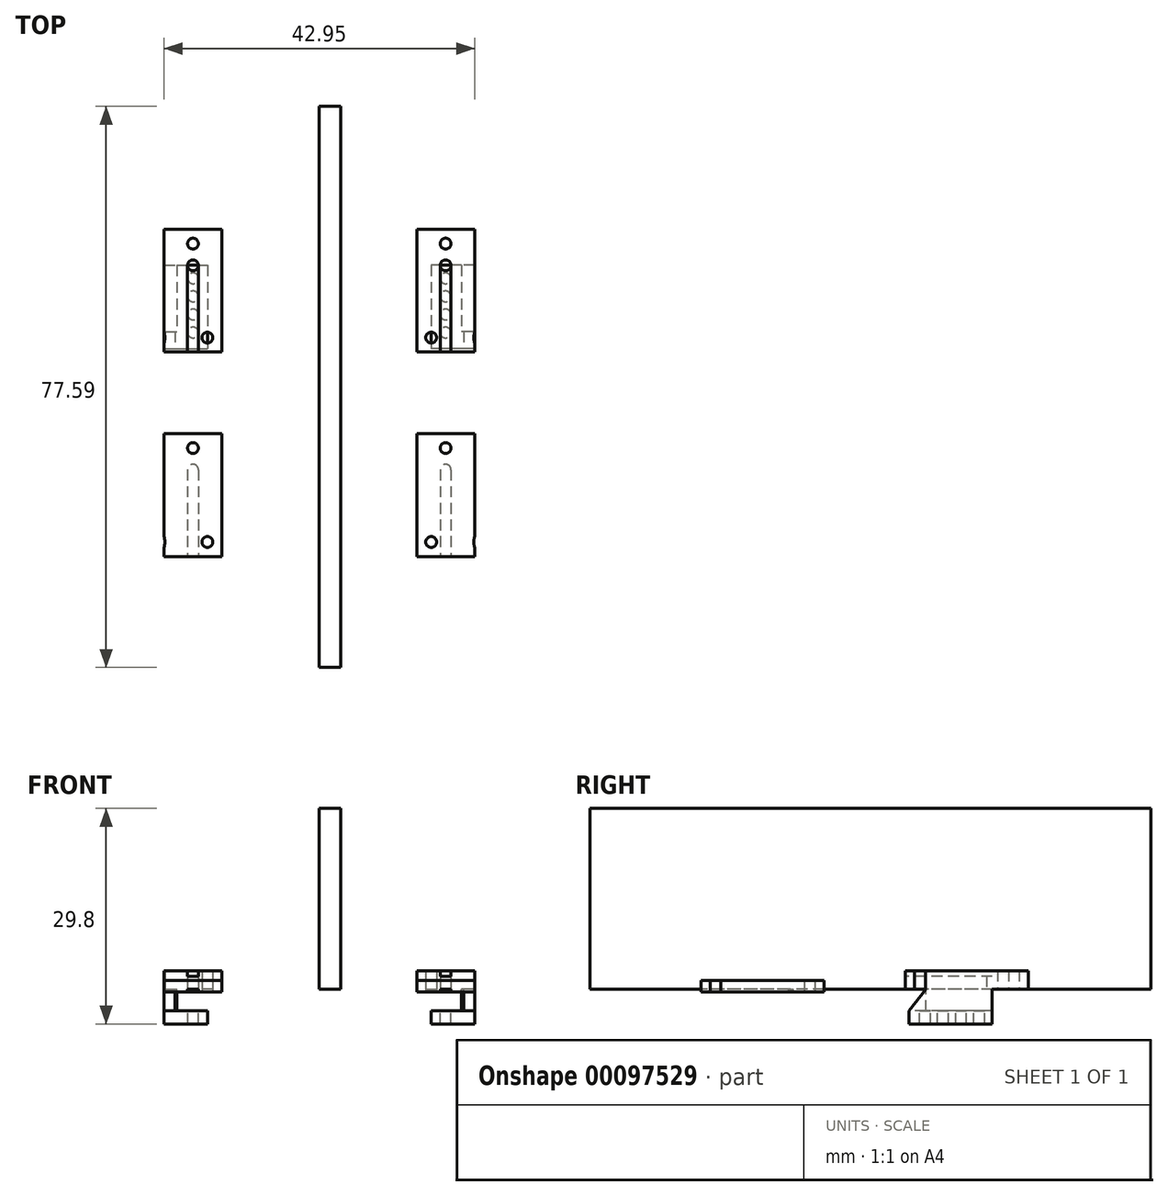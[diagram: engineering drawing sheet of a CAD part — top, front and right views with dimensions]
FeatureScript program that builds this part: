
annotation { "Feature Type Name" : "Feature", "Feature Type Description" : "" }
export const myFeature = defineFeature(function(context is Context, id is Id, definition is map)
    precondition{}
    {
        {
            var Q0;
            Q0=qCreatedBy(makeId("Top.planeOp"),FACE);
            var sketch = newSketch(context, id + "F0", { "sketchPlane" : qUnion([Q0])});
            skLineSegment(sketch, "E0.bottom", {"start": v(-5.2, 9) * mm, "end": v(2.8, 9) * mm});
            skLineSegment(sketch, "E0.top", {"start": v(-5.2, -8) * mm, "end": v(2.8, -8) * mm});
            skLineSegment(sketch, "E0.left", {"start": v(-5.2, 9) * mm, "end": v(-5.2, -5.26) * mm});
            skLineSegment(sketch, "E0.right", {"start": v(2.8, 9) * mm, "end": v(2.8, -8) * mm});
            skLineSegment(sketch, "E1", {"start": v(2.8, 9) * mm, "end": v(2.8, 11) * mm, "construction": true});
            skLineSegment(sketch, "E2", {"start": v(2.8, 11) * mm, "end": v(-1.2, 11) * mm, "construction": true});
            skLineSegment(sketch, "E3", {"start": v(-1.2, 11) * mm, "end": v(-1.2, 4) * mm, "construction": true});
            skCircle(sketch, "E4", {"center": v(-1.2, 4) * mm, "radius": 0.75 * mm});
            skLineSegment(sketch, "E5", {"start": v(-1.2, 9) * mm, "end": v(-1.2, 7) * mm, "construction": true});
            skCircle(sketch, "E6", {"center": v(-1.2, 7) * mm, "radius": 0.75 * mm});
            skLineSegment(sketch, "E7.bottom", {"start": v(2.8, -8) * mm, "end": v(0.8, -8) * mm, "construction": true});
            skLineSegment(sketch, "E7.top", {"start": v(2.8, -6) * mm, "end": v(0.8, -6) * mm, "construction": true});
            skLineSegment(sketch, "E7.left", {"start": v(2.8, -8) * mm, "end": v(2.8, -6) * mm, "construction": true});
            skLineSegment(sketch, "E7.right", {"start": v(0.8, -8) * mm, "end": v(0.8, -6) * mm, "construction": true});
            skCircle(sketch, "E8", {"center": v(0.8, -6) * mm, "radius": 0.75 * mm});
            skLineSegment(sketch, "E9", {"start": v(0.8, -6.76) * mm, "end": v(-5.2, -6.76) * mm, "construction": true});
            skLineSegment(sketch, "E10.MirrorCS", {"start": v(0.8, -5.26) * mm, "end": v(-5.2, -5.26) * mm, "construction": true});
            skArc(sketch, "E11", {"start": v(-5.2, -6.76) * mm, "mid": v(-5.1, -6) * mm, "end": v(-5.2, -5.26) * mm});
            skLineSegment(sketch, "E12.trimOffspring", {"start": v(-5.2, -6.76) * mm, "end": v(-5.2, -8) * mm});
            skLineSegment(sketch, "E13.0.1.0", {"start": v(0.8, -33.52) * mm, "end": v(-5.2, -33.52) * mm, "construction": true});
            skLineSegment(sketch, "E13.0.1.1", {"start": v(-5.2, -36.27) * mm, "end": v(2.8, -36.27) * mm});
            skLineSegment(sketch, "E13.0.1.2", {"start": v(0.8, -35.02) * mm, "end": v(-5.2, -35.02) * mm, "construction": true});
            skLineSegment(sketch, "E13.0.1.3", {"start": v(-1.2, -19.27) * mm, "end": v(-1.2, -21.27) * mm, "construction": true});
            skLineSegment(sketch, "E13.0.1.4", {"start": v(-5.2, -19.27) * mm, "end": v(-5.2, -33.52) * mm});
            skLineSegment(sketch, "E13.0.1.5", {"start": v(-5.2, -19.27) * mm, "end": v(2.8, -19.27) * mm});
            skLineSegment(sketch, "E13.0.1.6", {"start": v(2.8, -34.27) * mm, "end": v(0.8, -34.27) * mm, "construction": true});
            skCircle(sketch, "E13.0.1.7", {"center": v(0.8, -34.27) * mm, "radius": 0.75 * mm});
            skCircle(sketch, "E13.0.1.8", {"center": v(-1.2, -21.27) * mm, "radius": 0.75 * mm});
            skArc(sketch, "E13.0.1.9", {"start": v(-5.2, -35.02) * mm, "mid": v(-5.1, -34.27) * mm, "end": v(-5.2, -33.52) * mm});
            skLineSegment(sketch, "E13.0.1.10", {"start": v(2.8, -19.27) * mm, "end": v(2.8, -36.27) * mm});
            skLineSegment(sketch, "E13.0.1.12", {"start": v(0.8, -36.27) * mm, "end": v(0.8, -34.27) * mm, "construction": true});
            skLineSegment(sketch, "E13.0.1.13", {"start": v(2.8, -36.27) * mm, "end": v(0.8, -36.27) * mm, "construction": true});
            skLineSegment(sketch, "E13.0.1.14", {"start": v(2.8, -36.27) * mm, "end": v(2.8, -34.27) * mm, "construction": true});
            skLineSegment(sketch, "E13.0.1.15", {"start": v(-5.2, -35.02) * mm, "end": v(-5.2, -36.27) * mm});
            skLineSegment(sketch, "E13.direction1", {"start": v(-5.2, -5.26) * mm, "end": v(19.8, -5.26) * mm, "construction": true});
            skLineSegment(sketch, "E13.direction2", {"start": v(-5.2, -5.26) * mm, "end": v(-5.2, -33.52) * mm, "construction": true});
            skLineSegment(sketch, "E14", {"start": v(-1.2, -24.27) * mm, "end": v(2.8, -24.27) * mm, "construction": true});
            skCircle(sketch, "E15", {"center": v(-1.2, -24.27) * mm, "radius": 0.75 * mm});
            skLineSegment(sketch, "E16", {"start": v(-0.46, -24.27) * mm, "end": v(-0.46, -36.27) * mm});
            skLineSegment(sketch, "E17", {"start": v(-1.2, -24.27) * mm, "end": v(-1.2, -23.52) * mm, "construction": true});
            skLineSegment(sketch, "E18.MirrorCS", {"start": v(-1.96, -24.27) * mm, "end": v(-1.96, -36.27) * mm});
            skLineSegment(sketch, "E19.bottom", {"start": v(16.27, 25.97) * mm, "end": v(19.26, 25.97) * mm});
            skLineSegment(sketch, "E19.top", {"start": v(16.27, -51.62) * mm, "end": v(19.26, -51.62) * mm});
            skLineSegment(sketch, "E19.left", {"start": v(16.27, 25.97) * mm, "end": v(16.27, -51.62) * mm});
            skLineSegment(sketch, "E19.right", {"start": v(19.26, 25.97) * mm, "end": v(19.26, -51.62) * mm});
            skSolve(sketch);
        }
        {
            var Q0;
            Q0=makeQuery(id+"F0.imprint","IMPRINT",FACE,{"disambiguationData":[TD([[makeQuery(id+"F0.imprint","IMPRINT",EDGE,{"derivedFrom":sQuery(id+"F0.wireOp",EDGE,"E0.bottom")}),-1.0]])]});
            extrude(context, id + "F1", {"entities" : qUnion([Q0]), "depth" : 1.8 * mm});
        }
        {
            var Q0;
            Q0=makeQuery(id+"F1.opExtrude","CAP_FACE",FACE,{"disambiguationData":[OSD([sQuery(id+"F0.wireOp",EDGE,"E0.bottom"),sQuery(id+"F0.wireOp",EDGE,"E0.top"),sQuery(id+"F0.wireOp",EDGE,"E0.left"),sQuery(id+"F0.wireOp",EDGE,"E0.right"),sQuery(id+"F0.wireOp",EDGE,"E4")])],"isStart":false});
            var sketch = newSketch(context, id + "F2", { "sketchPlane" : qUnion([Q0])});
            skLineSegment(sketch, "E20", {"start": v(-1.2, 4) * mm, "end": v(8.32, 4) * mm, "construction": true});
            skLineSegment(sketch, "E21", {"start": v(-0.46, 4) * mm, "end": v(-0.46, -8) * mm});
            skLineSegment(sketch, "E22", {"start": v(-1.2, 4) * mm, "end": v(-1.2, 9) * mm, "construction": true});
            skLineSegment(sketch, "E23.MirrorCS", {"start": v(-1.96, 4) * mm, "end": v(-1.96, -8) * mm});
            skSolve(sketch);
        }
        {
            var Q0;
            {var subQ1=sQuery(id+"F2.wireOp",EDGE,"E21");Q0=makeQuery(id+"F2.imprint","IMPRINT",FACE,{"disambiguationData":[TD([[makeQuery(id+"F2.imprint","IMPRINT",EDGE,{"derivedFrom":subQ1}),1.0]])]});}
            extrude(context, id + "F3", {"entities" : qUnion([Q0]), "operationType" : NewBodyOperationType.ADD, "depth" : 0.75 * mm});
        }
        {
            var Q0;
            Q0=makeQuery(id+"F1.opExtrude","CAP_FACE",FACE,{"disambiguationData":[OSD([sQuery(id+"F0.wireOp",EDGE,"E0.bottom"),sQuery(id+"F0.wireOp",EDGE,"E0.top"),sQuery(id+"F0.wireOp",EDGE,"E0.left"),sQuery(id+"F0.wireOp",EDGE,"E0.right"),sQuery(id+"F0.wireOp",EDGE,"E4")])],"isStart":true});
            var sketch = newSketch(context, id + "F4", { "sketchPlane" : qUnion([Q0])});
            skLineSegment(sketch, "E24", {"start": v(-5.2, -9) * mm, "end": v(-3.7, -9) * mm, "construction": true});
            skPoint(sketch, "E24.endSnap0", {"position": v(-1.2, -9) * mm});
            skLineSegment(sketch, "E25", {"start": v(-5.2, 5.26) * mm, "end": v(-5.2, 5.16) * mm, "construction": true});
            skLineSegment(sketch, "E26", {"start": v(-5.2, 5.16) * mm, "end": v(-3.4, 5.16) * mm});
            skLineSegment(sketch, "E27", {"start": v(-5.2, -9) * mm, "end": v(-5.2, -4) * mm, "construction": true});
            skLineSegment(sketch, "E28", {"start": v(-5.2, -4) * mm, "end": v(-3.4, -4) * mm});
            skLineSegment(sketch, "E29", {"start": v(-3.4, -4) * mm, "end": v(-3.4, 5.16) * mm});
            skSolve(sketch);
        }
        {
            var Q0;
            Q0=makeQuery(id+"F0.imprint","IMPRINT",FACE,{"disambiguationData":[TD([[makeQuery(id+"F0.imprint","IMPRINT",EDGE,{"derivedFrom":sQuery(id+"F0.wireOp",EDGE,"E13.0.1.4")}),1.0]])]});
            var Q1;
            {var subQ0=sQuery(id+"F0.wireOp",EDGE,"MRaOlkRU-Fsrc-L5Ae-Ih45-m6OzS7PlfYht");Q1=makeQuery(id+"F0.imprint","IMPRINT",FACE,{"disambiguationData":[TD([[makeQuery(id+"F0.imprint","IMPRINT",EDGE,{"derivedFrom":subQ0}),1.0]])]});}
            var Q2;
            {var subQ0=sQuery(id+"F0.wireOp",EDGE,"E16");Q2=makeQuery(id+"F0.imprint","IMPRINT",FACE,{"disambiguationData":[TD([[makeQuery(id+"F0.imprint","IMPRINT",EDGE,{"derivedFrom":subQ0}),-1.0]])]});}
            var Q3;
            {var subQ0=sQuery(id+"F0.wireOp",EDGE,"E15");var subQ1=makeQuery(id+"F0.imprint","INTERSECT",VERTEX,{"derivedFrom":[subQ0,sQuery(id+"F0.wireOp",EDGE,"E16")]});Q3=makeQuery(id+"F0.imprint","IMPRINT",FACE,{"disambiguationData":[TD([[makeQuery(id+"F0.imprint","IMPRINT",EDGE,{"disambiguationData":[TD([[subQ1,-1.0]])],"derivedFrom":subQ0}),1.0]])]});}
            extrude(context, id + "F5", {"entities" : qUnion([Q0, Q1, Q2, Q3]), "depth" : 1.2 * mm});
        }
        {
            var Q0;
            Q0=makeQuery(id+"F0.imprint","IMPRINT",FACE,{"disambiguationData":[TD([[makeQuery(id+"F0.imprint","IMPRINT",EDGE,{"derivedFrom":sQuery(id+"F0.wireOp",EDGE,"E13.0.1.4")}),1.0]])]});
            extrude(context, id + "F6", {"entities" : qUnion([Q0]), "operationType" : NewBodyOperationType.ADD, "oppositeDirection" : true, "depth" : 0.4 * mm});
        }
        {
            var Q0;
            {var subQ0=sQuery(id+"F4.wireOp",EDGE,"E26");Q0=makeQuery(id+"F4.imprint","IMPRINT",FACE,{"disambiguationData":[TD([[makeQuery(id+"F4.imprint","IMPRINT",EDGE,{"derivedFrom":subQ0}),-1.0]])]});}
            extrude(context, id + "F7", {"entities" : qUnion([Q0]), "operationType" : NewBodyOperationType.ADD, "depth" : 3 * mm});
        }
        {
            var Q0;
            Q0=makeQuery(id+"F7.opExtrude","CAP_FACE",FACE,{"disambiguationData":[OSD([sQuery(id+"F0.wireOp",EDGE,"E0.left"),sQuery(id+"F4.wireOp",EDGE,"E26"),sQuery(id+"F4.wireOp",EDGE,"E28"),sQuery(id+"F4.wireOp",EDGE,"E29")])],"isStart":false});
            var sketch = newSketch(context, id + "F8", { "sketchPlane" : qUnion([Q0])});
            skLineSegment(sketch, "E30.bottom", {"start": v(-5.2, -4) * mm, "end": v(0.8, -4) * mm});
            skLineSegment(sketch, "E30.top", {"start": v(-5.2, 7.5) * mm, "end": v(0.8, 7.5) * mm});
            skLineSegment(sketch, "E30.left", {"start": v(-5.2, -4) * mm, "end": v(-5.2, 7.5) * mm});
            skLineSegment(sketch, "E30.right", {"start": v(0.8, -4) * mm, "end": v(0.8, 7.5) * mm});
            skLineSegment(sketch, "E31", {"start": v(-1.2, -4) * mm, "end": v(-1.2, 7.5) * mm, "construction": true});
            skLineSegment(sketch, "E32", {"start": v(0.8, 7.5) * mm, "end": v(8.74, 7.5) * mm, "construction": true});
            skLineSegment(sketch, "E33", {"start": v(0.8, -4) * mm, "end": v(15.08, -4) * mm, "construction": true});
            skLineSegment(sketch, "E34", {"start": v(15.08, -4) * mm, "end": v(15.08, -2.2) * mm, "construction": true});
            skLineSegment(sketch, "E35", {"start": v(15.08, -2.2) * mm, "end": v(-10.13, -2.2) * mm, "construction": true});
            skCircle(sketch, "E36", {"center": v(-1.2, -2.2) * mm, "radius": 0.75 * mm});
            skLineSegment(sketch, "E37", {"start": v(15.08, -2.2) * mm, "end": v(15.08, 0.3) * mm, "construction": true});
            skLineSegment(sketch, "E38", {"start": v(15.08, 0.3) * mm, "end": v(-9.47, 0.3) * mm, "construction": true});
            skCircle(sketch, "E39", {"center": v(-1.2, 0.3) * mm, "radius": 0.75 * mm});
            skLineSegment(sketch, "E40", {"start": v(15.08, 0.3) * mm, "end": v(15.08, 2.8) * mm, "construction": true});
            skLineSegment(sketch, "E41", {"start": v(15.08, 2.8) * mm, "end": v(-9.74, 2.8) * mm, "construction": true});
            skCircle(sketch, "E42", {"center": v(-1.2, 2.8) * mm, "radius": 0.75 * mm});
            skLineSegment(sketch, "E43", {"start": v(15.08, 2.8) * mm, "end": v(15.08, 5.3) * mm, "construction": true});
            skLineSegment(sketch, "E44", {"start": v(15.08, 5.3) * mm, "end": v(-8.87, 5.3) * mm, "construction": true});
            skCircle(sketch, "E45", {"center": v(-1.2, 5.3) * mm, "radius": 0.75 * mm});
            skLineSegment(sketch, "E46", {"start": v(-1.19, -4) * mm, "end": v(-1.19, 12.58) * mm, "construction": true});
            skSolve(sketch);
        }
        {
            var Q0;
            {var subQ0=sQuery(id+"F8.wireOp",EDGE,"E30.top");Q0=makeQuery(id+"F8.imprint","IMPRINT",FACE,{"disambiguationData":[TD([[makeQuery(id+"F8.imprint","IMPRINT",EDGE,{"derivedFrom":subQ0}),-1.0]])]});}
            var Q1;
            {var subQ4=makeQuery(id+"F7.opExtrude","CAP_EDGE",EDGE,{"disambiguationData":[OSD([sQuery(id+"F4.wireOp",EDGE,"E26")])],"isStart":false});Q1=makeQuery(id+"F8.imprint","IMPRINT",FACE,{"disambiguationData":[TD([[makeQuery(id+"F8.imprint","IMPRINT",EDGE,{"derivedFrom":subQ4}),-1.0]])]});}
            extrude(context, id + "F9", {"entities" : qUnion([Q0, Q1]), "operationType" : NewBodyOperationType.ADD, "depth" : 1.8 * mm});
        }
        {
            var Q0;
            {var subQ0=sQuery(id+"F0.wireOp",EDGE,"E0.left");Q0=makeQuery(id+"F9.boolean.opBoolean","MERGE",FACE,{"derivedFrom":[makeQuery(id+"F7.boolean.opBoolean","MERGE",FACE,{"derivedFrom":[makeQuery(id+"F3.boolean.opBoolean","MERGE",FACE,{"derivedFrom":[makeQuery(id+"F1.opExtrude","SWEPT_FACE",FACE,{"disambiguationData":[OSD([subQ0])]}),makeQuery(id+"F3.opExtrude","SWEPT_FACE",FACE,{"disambiguationData":[OSD([subQ0])]})]}),makeQuery(id+"F7.opExtrude","SWEPT_FACE",FACE,{"disambiguationData":[OSD([subQ0])]})]}),makeQuery(id+"F9.opExtrude","SWEPT_FACE",FACE,{"disambiguationData":[OSD([sQuery(id+"F8.wireOp",EDGE,"E30.left")])]})]});}
            var sketch = newSketch(context, id + "F10", { "sketchPlane" : qUnion([Q0])});
            skLineSegment(sketch, "E47", {"start": v(5.16, -3) * mm, "end": v(7.5, -3) * mm});
            skLineSegment(sketch, "E48", {"start": v(7.5, -3) * mm, "end": v(5.16, 0) * mm});
            skLineSegment(sketch, "E49", {"start": v(5.16, 0) * mm, "end": v(5.16, -3) * mm});
            skSolve(sketch);
        }
        {
            var Q0;
            Q0=makeQuery(id+"F10.imprint","IMPRINT",FACE,{"disambiguationData":[TD([[makeQuery(id+"F10.imprint","IMPRINT",EDGE,{"derivedFrom":sQuery(id+"F10.wireOp",EDGE,"E47")}),1.0]])]});
            extrude(context, id + "F11", {"entities" : qUnion([Q0]), "operationType" : NewBodyOperationType.ADD, "oppositeDirection" : true, "depth" : 1.5 * mm});
        }
        {
            var Q0;
            Q0=makeQuery(id+"F0.imprint","IMPRINT",FACE,{"disambiguationData":[TD([[makeQuery(id+"F0.imprint","IMPRINT",EDGE,{"derivedFrom":sQuery(id+"F0.wireOp",EDGE,"E19.bottom")}),-1.0]])]});
            extrude(context, id + "F12", {"entities" : qUnion([Q0]), "depth" : 25 * mm});
        }
        {
            var Q0;
            Q0=makeQuery(id+"F5.opExtrude","SWEPT_BODY",BODY,{"disambiguationData":[OSD([sQuery(id+"F0.wireOp",EDGE,"E13.0.1.1"),sQuery(id+"F0.wireOp",EDGE,"E13.0.1.4"),sQuery(id+"F0.wireOp",EDGE,"E13.0.1.5"),sQuery(id+"F0.wireOp",EDGE,"E13.0.1.7"),sQuery(id+"F0.wireOp",EDGE,"E13.0.1.8"),sQuery(id+"F0.wireOp",EDGE,"E13.0.1.9"),sQuery(id+"F0.wireOp",EDGE,"E13.0.1.10"),sQuery(id+"F0.wireOp",EDGE,"E13.0.1.15")])]});
            var Q1;
            Q1=makeQuery(id+"F1.opExtrude","SWEPT_BODY",BODY,{"disambiguationData":[OSD([sQuery(id+"F0.wireOp",EDGE,"E0.bottom"),sQuery(id+"F0.wireOp",EDGE,"E0.top"),sQuery(id+"F0.wireOp",EDGE,"E0.left"),sQuery(id+"F0.wireOp",EDGE,"E0.right"),sQuery(id+"F0.wireOp",EDGE,"E4"),sQuery(id+"F0.wireOp",EDGE,"E6"),sQuery(id+"F0.wireOp",EDGE,"E8"),sQuery(id+"F0.wireOp",EDGE,"E11"),sQuery(id+"F0.wireOp",EDGE,"E12.trimOffspring")])]});
            var Q2;
            Q2=makeQuery(id+"F12.opExtrude","SWEPT_FACE",FACE,{"disambiguationData":[OSD([sQuery(id+"F0.wireOp",EDGE,"E19.left")])]});
            mirror(context, id + "F13", {"entities" : qUnion([Q0, Q1]), "mirrorPlane" : qUnion([Q2])});
        }
    });
